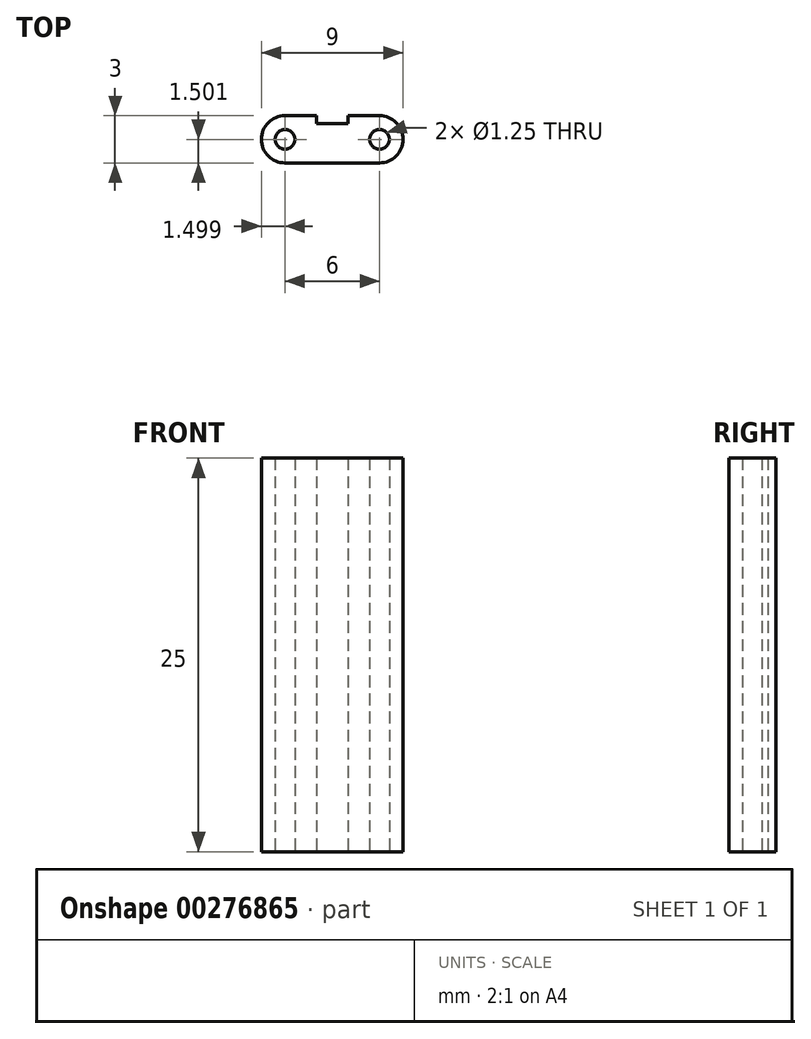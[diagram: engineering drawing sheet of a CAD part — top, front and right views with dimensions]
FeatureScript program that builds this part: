
annotation { "Feature Type Name" : "Feature", "Feature Type Description" : "" }
export const myFeature = defineFeature(function(context is Context, id is Id, definition is map)
    precondition{}
    {
        {
            var Q0;
            Q0=qCreatedBy(makeId("Top.planeOp"),FACE);
            var sketch = newSketch(context, id + "F0", { "sketchPlane" : qUnion([Q0])});
            skCircle(sketch, "E0", {"center": v(-40.48, 29.04) * mm, "radius": 0.63 * mm});
            skArc(sketch, "E1", {"start": v(-40.48, 27.54) * mm, "mid": v(-38.98, 29.04) * mm, "end": v(-40.48, 30.54) * mm});
            skCircle(sketch, "E2", {"center": v(-46.48, 29.04) * mm, "radius": 0.62 * mm});
            skArc(sketch, "E3", {"start": v(-46.48, 30.54) * mm, "mid": v(-47.98, 29.04) * mm, "end": v(-46.48, 27.54) * mm});
            skLineSegment(sketch, "E4", {"start": v(-46.48, 27.54) * mm, "end": v(-40.48, 27.54) * mm});
            skLineSegment(sketch, "E5", {"start": v(-46.48, 30.54) * mm, "end": v(-44.48, 30.54) * mm});
            skLineSegment(sketch, "E6", {"start": v(-44.48, 30.54) * mm, "end": v(-44.48, 30.04) * mm});
            skLineSegment(sketch, "E7", {"start": v(-44.48, 30.04) * mm, "end": v(-42.48, 30.04) * mm});
            skLineSegment(sketch, "E8", {"start": v(-42.48, 30.04) * mm, "end": v(-42.48, 30.54) * mm});
            skLineSegment(sketch, "E9.trimOffspring", {"start": v(-42.48, 30.54) * mm, "end": v(-40.48, 30.54) * mm});
            skSolve(sketch);
        }
        {
            var Q0;
            Q0 = qSketchRegion(id + "F0", true);
            extrude(context, id + "F1", {"entities" : qUnion([Q0]), "depth" : 25 * mm});
        }
    });
